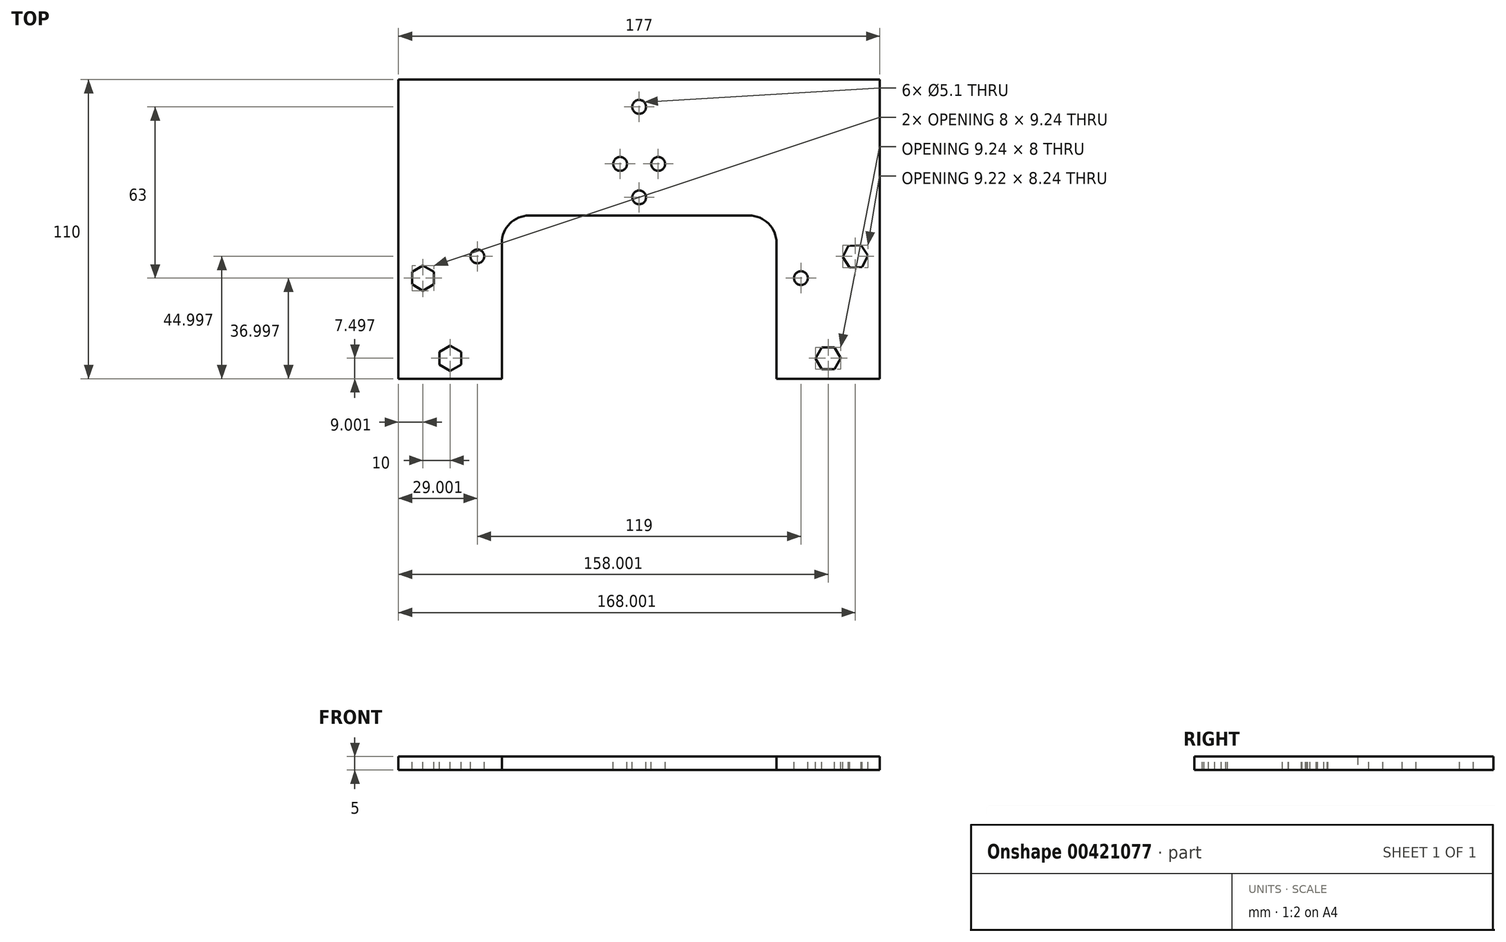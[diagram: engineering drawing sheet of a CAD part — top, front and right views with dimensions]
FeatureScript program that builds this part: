
annotation { "Feature Type Name" : "Feature", "Feature Type Description" : "" }
export const myFeature = defineFeature(function(context is Context, id is Id, definition is map)
    precondition{}
    {
        {
            var Q0;
            Q0=qCreatedBy(makeId("Top.planeOp"),FACE);
            var sketch = newSketch(context, id + "F0", { "sketchPlane" : qUnion([Q0])});
            skLineSegment(sketch, "E0.bottom", {"start": v(-92.32, 58.53) * mm, "end": v(84.68, 58.53) * mm});
            skLineSegment(sketch, "E0.top", {"start": v(-44.32, 8.53) * mm, "end": v(36.68, 8.53) * mm});
            skLineSegment(sketch, "E0.left", {"start": v(-92.32, 58.53) * mm, "end": v(-92.32, 8.53) * mm});
            skLineSegment(sketch, "E0.right", {"start": v(84.68, 58.53) * mm, "end": v(84.68, 8.53) * mm});
            skLineSegment(sketch, "E1.top", {"start": v(-92.32, -51.47) * mm, "end": v(-54.32, -51.47) * mm});
            skLineSegment(sketch, "E1.left", {"start": v(-92.32, 8.53) * mm, "end": v(-92.32, -51.47) * mm});
            skLineSegment(sketch, "E1.right", {"start": v(-54.32, -1.47) * mm, "end": v(-54.32, -51.47) * mm});
            skLineSegment(sketch, "E2.top", {"start": v(84.68, -51.47) * mm, "end": v(46.68, -51.47) * mm});
            skLineSegment(sketch, "E2.left", {"start": v(84.68, 8.53) * mm, "end": v(84.68, -51.47) * mm});
            skLineSegment(sketch, "E2.right", {"start": v(46.68, -1.47) * mm, "end": v(46.68, -51.47) * mm});
            skPoint(sketch, "E3.visualSharp", {"position": v(-54.32, 8.53) * mm});
            skArc(sketch, "E3.filletArc", {"start": v(-44.32, 8.53) * mm, "mid": v(-51.39, 5.6) * mm, "end": v(-54.32, -1.47) * mm});
            skPoint(sketch, "E4.visualSharp", {"position": v(46.68, 8.53) * mm});
            skArc(sketch, "E4.filletArc", {"start": v(46.68, -1.47) * mm, "mid": v(43.75, 5.6) * mm, "end": v(36.68, 8.53) * mm});
            skSolve(sketch);
        }
        {
            var Q0;
            Q0 = qSketchRegion(id + "F0", true);
            extrude(context, id + "F1", {"entities" : qUnion([Q0]), "depth" : 5 * mm});
        }
        {
            var Q0;
            Q0=makeQuery(id+"F1.opExtrude","CAP_FACE",FACE,{"disambiguationData":[OSD([sQuery(id+"F0.wireOp",EDGE,"E0.bottom"),sQuery(id+"F0.wireOp",EDGE,"E0.top"),sQuery(id+"F0.wireOp",EDGE,"E0.left"),sQuery(id+"F0.wireOp",EDGE,"E0.right")])],"isStart":false});
            var sketch = newSketch(context, id + "F2", { "sketchPlane" : qUnion([Q0])});
            skPoint(sketch, "E5", {"position": v(-3.82, 48.53) * mm});
            skPoint(sketch, "E6", {"position": v(-3.82, 15.23) * mm});
            skPoint(sketch, "E7", {"position": v(-10.82, 27.53) * mm});
            skPoint(sketch, "E8", {"position": v(3.18, 27.53) * mm});
            skSolve(sketch);
        }
        {
            var Q0;
            Q0=sQuery(id+"F2.wireOp",VERTEX,"E7");
            var Q1;
            Q1=sQuery(id+"F2.wireOp",VERTEX,"E5");
            var Q2;
            Q2=sQuery(id+"F2.wireOp",VERTEX,"E8");
            var Q3;
            Q3=sQuery(id+"F2.wireOp",VERTEX,"E6");
            var Q4;
            Q4=makeQuery(id+"F1.opExtrude","SWEPT_BODY",BODY,{"disambiguationData":[OSD([sQuery(id+"F0.wireOp",EDGE,"E0.bottom"),sQuery(id+"F0.wireOp",EDGE,"E0.top"),sQuery(id+"F0.wireOp",EDGE,"E0.left"),sQuery(id+"F0.wireOp",EDGE,"E0.right")])]});
            hole(context, id + "F3", {"style" : HoleStyle.SIMPLE, "endStyle" : HoleEndStyle.THROUGH, "standardTappedOrClearance" : lookupTablePath({ "standard" : "ISO", "size" : "5.1", "type" : "Drilled" }), "standardBlindInLast" : lookupTablePath({ "standard" : "ISO", "size" : "5.1", "type" : "Drilled" }), "holeDiameter" : 5.1 * mm, "tappedDepth" : 12.7 * mm, "tapClearance" : 3, "locations" : qUnion([Q0, Q1, Q2, Q3]), "scope" : qUnion([Q4])});
        }
        {
            var Q0;
            Q0=makeQuery(id+"F1.opExtrude","CAP_FACE",FACE,{"disambiguationData":[OSD([sQuery(id+"F0.wireOp",EDGE,"E0.bottom"),sQuery(id+"F0.wireOp",EDGE,"E0.top"),sQuery(id+"F0.wireOp",EDGE,"E0.left"),sQuery(id+"F0.wireOp",EDGE,"E0.right"),sQuery(id+"F0.wireOp",EDGE,"E1.top"),sQuery(id+"F0.wireOp",EDGE,"E1.left"),sQuery(id+"F0.wireOp",EDGE,"E1.right"),sQuery(id+"F0.wireOp",EDGE,"E2.top"),sQuery(id+"F0.wireOp",EDGE,"E2.left"),sQuery(id+"F0.wireOp",EDGE,"E2.right"),sQuery(id+"F0.wireOp",EDGE,"E3.filletArc"),sQuery(id+"F0.wireOp",EDGE,"E4.filletArc")])],"isStart":false});
            var sketch = newSketch(context, id + "F4", { "sketchPlane" : qUnion([Q0])});
            skPoint(sketch, "E9", {"position": v(-73.32, -43.97) * mm});
            skPoint(sketch, "E10", {"position": v(65.68, -43.97) * mm});
            skPoint(sketch, "E11", {"position": v(-83.32, -14.47) * mm});
            skPoint(sketch, "E12", {"position": v(-63.32, -6.47) * mm});
            skPoint(sketch, "E13", {"position": v(55.68, -14.47) * mm});
            skPoint(sketch, "E14", {"position": v(75.68, -6.47) * mm});
            skCircle(sketch, "E15.cCircle", {"center": v(-83.32, -14.47) * mm, "radius": 4 * mm, "construction": true});
            skLineSegment(sketch, "E15.0", {"start": v(-79.32, -12.16) * mm, "end": v(-79.32, -16.78) * mm});
            skLineSegment(sketch, "E15.1", {"start": v(-79.32, -16.78) * mm, "end": v(-83.32, -19.1) * mm});
            skLineSegment(sketch, "E15.2", {"start": v(-83.32, -19.1) * mm, "end": v(-87.32, -16.78) * mm});
            skLineSegment(sketch, "E15.3", {"start": v(-87.32, -16.78) * mm, "end": v(-87.32, -12.16) * mm});
            skLineSegment(sketch, "E15.4", {"start": v(-87.32, -12.16) * mm, "end": v(-83.32, -9.85) * mm});
            skLineSegment(sketch, "E15.5", {"start": v(-83.32, -9.85) * mm, "end": v(-79.32, -12.16) * mm});
            skPoint(sketch, "E15.0.midPoint", {"position": v(-79.32, -14.47) * mm});
            skCircle(sketch, "E16.cCircle", {"center": v(-73.32, -43.97) * mm, "radius": 4 * mm, "construction": true});
            skLineSegment(sketch, "E16.0", {"start": v(-69.32, -41.66) * mm, "end": v(-69.32, -46.28) * mm});
            skLineSegment(sketch, "E16.1", {"start": v(-69.32, -46.28) * mm, "end": v(-73.32, -48.6) * mm});
            skLineSegment(sketch, "E16.2", {"start": v(-73.32, -48.6) * mm, "end": v(-77.32, -46.28) * mm});
            skLineSegment(sketch, "E16.3", {"start": v(-77.32, -46.28) * mm, "end": v(-77.32, -41.66) * mm});
            skLineSegment(sketch, "E16.4", {"start": v(-77.32, -41.66) * mm, "end": v(-73.32, -39.35) * mm});
            skLineSegment(sketch, "E16.5", {"start": v(-73.32, -39.35) * mm, "end": v(-69.32, -41.66) * mm});
            skPoint(sketch, "E16.0.midPoint", {"position": v(-69.32, -43.97) * mm});
            skCircle(sketch, "E17.cCircle", {"center": v(75.68, -6.47) * mm, "radius": 4 * mm, "construction": true});
            skLineSegment(sketch, "E17.0", {"start": v(73.59, -10.6) * mm, "end": v(71.07, -6.72) * mm});
            skLineSegment(sketch, "E17.1", {"start": v(71.07, -6.72) * mm, "end": v(73.16, -2.6) * mm});
            skLineSegment(sketch, "E17.2", {"start": v(73.16, -2.6) * mm, "end": v(77.77, -2.36) * mm});
            skLineSegment(sketch, "E17.3", {"start": v(77.77, -2.36) * mm, "end": v(80.3, -6.23) * mm});
            skLineSegment(sketch, "E17.4", {"start": v(80.3, -6.23) * mm, "end": v(78.2, -10.34) * mm});
            skLineSegment(sketch, "E17.5", {"start": v(78.2, -10.34) * mm, "end": v(73.59, -10.6) * mm});
            skPoint(sketch, "E17.0.midPoint", {"position": v(72.33, -8.66) * mm});
            skCircle(sketch, "E18.cCircle", {"center": v(65.68, -43.97) * mm, "radius": 4 * mm, "construction": true});
            skLineSegment(sketch, "E18.0", {"start": v(67.99, -39.97) * mm, "end": v(70.3, -43.97) * mm});
            skLineSegment(sketch, "E18.1", {"start": v(70.3, -43.97) * mm, "end": v(68, -47.97) * mm});
            skLineSegment(sketch, "E18.2", {"start": v(68, -47.97) * mm, "end": v(63.38, -47.98) * mm});
            skLineSegment(sketch, "E18.3", {"start": v(63.38, -47.98) * mm, "end": v(61.06, -43.98) * mm});
            skLineSegment(sketch, "E18.4", {"start": v(61.06, -43.98) * mm, "end": v(63.37, -39.98) * mm});
            skLineSegment(sketch, "E18.5", {"start": v(63.37, -39.98) * mm, "end": v(67.99, -39.97) * mm});
            skPoint(sketch, "E18.0.midPoint", {"position": v(69.14, -41.97) * mm});
            skCircle(sketch, "E19", {"center": v(-63.32, -6.47) * mm, "radius": 2.55 * mm});
            skCircle(sketch, "E20", {"center": v(55.68, -14.47) * mm, "radius": 2.55 * mm});
            skSolve(sketch);
        }
        {
            var Q0;
            Q0 = qSketchRegion(id + "F4", true);
            extrude(context, id + "F5", {"entities" : qUnion([Q0]), "operationType" : NewBodyOperationType.REMOVE, "oppositeDirection" : true, "depth" : 25 * mm});
        }
    });
